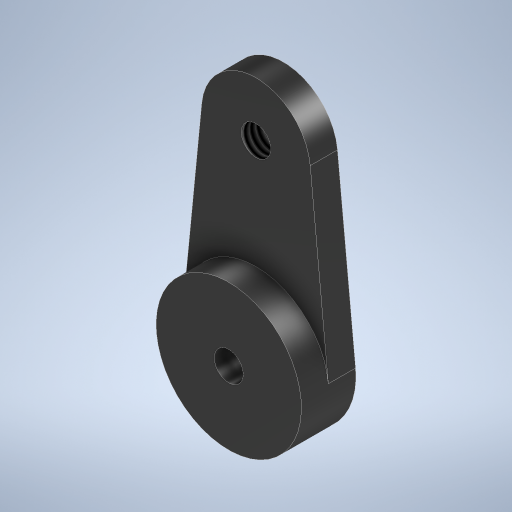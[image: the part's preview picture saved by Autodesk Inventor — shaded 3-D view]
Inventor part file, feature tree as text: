
AUTODESK INVENTOR PART (.ipt)
format: ipt  version: 2024.2 (Build 282272000, 272)  size: 282,112 bytes
history: native  units: mm
features: sketch x1, extrude x1, hole x1
ambient origin geometry x8: Origin, YZ Plane, XZ Plane, XY Plane, X Axis, Y Axis, Z Axis, Center Point
bodies: Solid1 (feature_tree)
feature tree (3):
  sketch  "Sketch1"  dims[d0=16.0mm d1=20.0mm d2=12.0mm d5=6.0mm d6=0.0mm d9=3.0mm d10=0.0mm d11=3.2mm d12=6.0mm d13=4.0mm d14=2.0mm d15=90.0deg d16=8.0mm d17=20.594885mm d18=3.242mm d19=8.0mm d20=4.0mm d21=2.0mm d22=90.0deg d23=8.0mm d24=20.594885mm d28=60.0deg d29=5.0mm d30=0.025mm d31=5.0mm d32=0.025mm]
  extrude  "Extrusion1"  Depth=20.0mm
  hole  "Phi3.2"  [1 undecoded]
note: 1 required parameter value undecoded (feature->parameter linkage not recoverable at this tier; creation-order binding heuristic only, values carry confidence <= 0.55)
